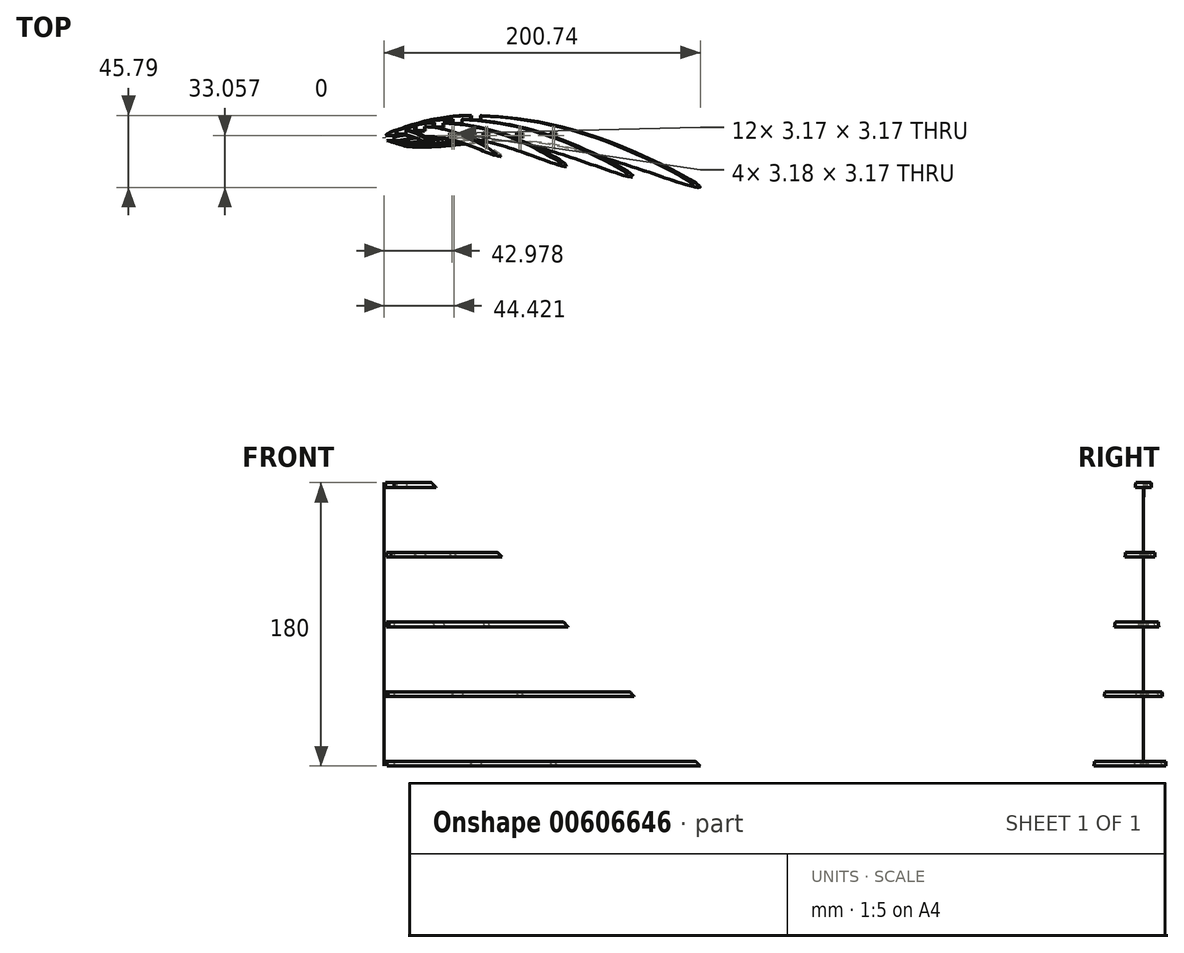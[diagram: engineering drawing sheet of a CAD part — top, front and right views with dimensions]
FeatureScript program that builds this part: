
annotation { "Feature Type Name" : "Feature", "Feature Type Description" : "" }
export const myFeature = defineFeature(function(context is Context, id is Id, definition is map)
    precondition{}
    {
        {
            var Q0;
            Q0=qCreatedBy(makeId("Top.planeOp"),FACE);
            var sketch = newSketch(context, id + "F0", { "sketchPlane" : qUnion([Q0])});
            skFitSpline(sketch, "E0", {"points": [v(6.7, -3.08) * mm, v(0, 0) * mm, v(27, 10.93) * mm, v(65.88, 14) * mm, v(142.55, -2.18) * mm, v(200.64, -31.37) * mm, v(115.71, -5.76) * mm, v(49.67, -4.11) * mm, v(16, -5.56) * mm, v(6.7, -3.08) * mm]});
            skLineSegment(sketch, "E1", {"start": v(52.43, 14.3) * mm, "end": v(52.43, 14.3) * mm});
            skSolve(sketch);
        }
        {
            var Q0;
            Q0=qCreatedBy(makeId("Top.planeOp"),FACE);
            cPlane(context, id + "F1", {"entities" : qUnion([Q0]), "cplaneType" : CPlaneType.OFFSET, "offset" : 180 * mm, "width" : 150 * mm, "height" : 150 * mm});
        }
        {
            var Q0;
            Q0=qCreatedBy(id+"F1.planeOp",FACE);
            var sketch = newSketch(context, id + "F2", { "sketchPlane" : qUnion([Q0])});
            skFitSpline(sketch, "E2", {"points": [v(0, 0) * mm, v(2.44, 2.88) * mm, v(10.73, 5.12) * mm, v(24.6, 0.41) * mm, v(30.02, -4.78) * mm, v(15.98, 1.36) * mm, v(4, -0.03) * mm, v(2.4, -0.47) * mm, v(0.9, -0.46) * mm, v(0, 0) * mm]});
            skSolve(sketch);
        }
        {
            var Q0;
            Q0=qCreatedBy(makeId("Right.planeOp"),FACE);
            var sketch = newSketch(context, id + "F3", { "sketchPlane" : qUnion([Q0])});
            skPoint(sketch, "E3.0", {"position": v(0, 180) * mm});
            skLineSegment(sketch, "E4", {"start": v(0, 180) * mm, "end": v(0, 0) * mm});
            skSolve(sketch);
        }
        {
            var Q0;
            Q0 = qSketchRegion(id + "F0", true);
            var Q1;
            Q1 = qSketchRegion(id + "F2", true);
            var Q2;
            Q2=sQuery(id+"F3.wireOp",EDGE,"E4");
            loft(context, id + "F4", {"addGuides" : true, "sheetProfilesArray" : [{ "sheetProfileEntities" : qUnion([Q0]) }, { "sheetProfileEntities" : qUnion([Q1]) }], "guidesArray" : [{ "guideEntities" : qUnion([Q2]), "guideDerivativeType" : LoftGuideDerivativeType.DEFAULT, "guideDerivativeMagnitude" : 1 }]});
        }
        {
            var Q0;
            Q0=makeQuery(id+"F2.imprint","IMPRINT",FACE,{"disambiguationData":[TD([[makeQuery(id+"F2.imprint","IMPRINT",EDGE,{"derivedFrom":sQuery(id+"F2.wireOp",EDGE,"E2")}),-1.0]])]});
            var sketch = newSketch(context, id + "F5", { "sketchPlane" : qUnion([Q0])});
            skLineSegment(sketch, "E5", {"start": v(10.64, 5.35) * mm, "end": v(13.82, 5.35) * mm});
            skLineSegment(sketch, "E6", {"start": v(13.82, 5.35) * mm, "end": v(13.82, 2.18) * mm});
            skLineSegment(sketch, "E7", {"start": v(13.82, 2.18) * mm, "end": v(7.47, 2.18) * mm});
            skLineSegment(sketch, "E8", {"start": v(7.47, 2.18) * mm, "end": v(7.47, 5.35) * mm});
            skLineSegment(sketch, "E9", {"start": v(7.47, 5.35) * mm, "end": v(10.64, 5.35) * mm});
            skSolve(sketch);
        }
        {
            var Q0;
            Q0=makeQuery(id+"F0.imprint","IMPRINT",FACE,{"disambiguationData":[TD([[makeQuery(id+"F0.imprint","IMPRINT",EDGE,{"derivedFrom":sQuery(id+"F0.wireOp",EDGE,"E0")}),-1.0]])]});
            var sketch = newSketch(context, id + "F6", { "sketchPlane" : qUnion([Q0])});
            skLineSegment(sketch, "E10", {"start": v(58.72, 14.54) * mm, "end": v(55.54, 14.54) * mm});
            skLineSegment(sketch, "E11", {"start": v(55.54, 14.54) * mm, "end": v(55.54, 11.36) * mm});
            skLineSegment(sketch, "E12", {"start": v(55.54, 11.36) * mm, "end": v(61.9, 11.36) * mm});
            skLineSegment(sketch, "E13", {"start": v(61.9, 11.36) * mm, "end": v(61.9, 14.54) * mm});
            skLineSegment(sketch, "E14", {"start": v(61.9, 14.54) * mm, "end": v(58.72, 14.54) * mm});
            skSolve(sketch);
        }
        {
            var Q0;
            Q0=sQuery(id+"F6.wireOp",VERTEX,"E11.start");
            var Q1;
            Q1=sQuery(id+"F6.wireOp",VERTEX,"E12.start");
            var Q2;
            Q2=sQuery(id+"F5.wireOp",VERTEX,"E8.start");
            cPlane(context, id + "F7", {"entities" : qUnion([Q0, Q1, Q2]), "cplaneType" : CPlaneType.THREE_POINT, "offset" : 25 * mm, "width" : 150 * mm, "height" : 150 * mm});
        }
        {
            var Q0;
            Q0=qCreatedBy(id+"F7.planeOp",FACE);
            var sketch = newSketch(context, id + "F8", { "sketchPlane" : qUnion([Q0])});
            skPoint(sketch, "E15.0", {"position": v(2.18, 171.98) * mm});
            skPoint(sketch, "E16.0", {"position": v(11.36, -14.33) * mm});
            skLineSegment(sketch, "E17", {"start": v(2.18, 171.98) * mm, "end": v(11.36, -14.33) * mm});
            skSolve(sketch);
        }
        {
            var Q0;
            Q0 = qSketchRegion(id + "F5", true);
            var Q1;
            Q1 = qSketchRegion(id + "F6", true);
            var Q2;
            Q2=sQuery(id+"F8.wireOp",EDGE,"E17");
            sweep(context, id + "F9", {"operationType" : NewBodyOperationType.REMOVE, "profiles" : qUnion([Q0, Q1]), "path" : qUnion([Q2])});
        }
        {
            var Q0;
            Q0=makeQuery(id+"F2.imprint","IMPRINT",FACE,{"disambiguationData":[TD([[makeQuery(id+"F2.imprint","IMPRINT",EDGE,{"derivedFrom":sQuery(id+"F2.wireOp",EDGE,"E2")}),-1.0]])]});
            var sketch = newSketch(context, id + "F10", { "sketchPlane" : qUnion([Q0])});
            skLineSegment(sketch, "E18", {"start": v(0, 0) * mm, "end": v(0, 1.59) * mm});
            skLineSegment(sketch, "E19", {"start": v(0, 1.59) * mm, "end": v(6.35, 1.59) * mm});
            skLineSegment(sketch, "E20", {"start": v(6.35, 1.59) * mm, "end": v(6.35, -1.59) * mm});
            skLineSegment(sketch, "E21", {"start": v(6.35, -1.59) * mm, "end": v(0, -1.59) * mm});
            skLineSegment(sketch, "E22", {"start": v(0, -1.59) * mm, "end": v(0, 0) * mm});
            skSolve(sketch);
        }
        {
            var Q0;
            Q0=makeQuery(id+"F0.imprint","IMPRINT",FACE,{"disambiguationData":[TD([[makeQuery(id+"F0.imprint","IMPRINT",EDGE,{"derivedFrom":sQuery(id+"F0.wireOp",EDGE,"E0")}),-1.0]])]});
            var sketch = newSketch(context, id + "F11", { "sketchPlane" : qUnion([Q0])});
            skLineSegment(sketch, "E23", {"start": v(0, 0) * mm, "end": v(0, 1.59) * mm});
            skLineSegment(sketch, "E24", {"start": v(0, 1.59) * mm, "end": v(3.18, 1.59) * mm});
            skLineSegment(sketch, "E25", {"start": v(3.18, 1.59) * mm, "end": v(3.18, -1.59) * mm});
            skLineSegment(sketch, "E26", {"start": v(3.18, -1.59) * mm, "end": v(0, -1.59) * mm});
            skLineSegment(sketch, "E27", {"start": v(0, -1.59) * mm, "end": v(0, 0) * mm});
            skSolve(sketch);
        }
        {
            var Q0;
            Q0=sQuery(id+"F11.wireOp",VERTEX,"E27.start");
            var Q1;
            Q1=sQuery(id+"F11.wireOp",VERTEX,"E24.start");
            var Q2;
            Q2=sQuery(id+"F10.wireOp",VERTEX,"E19.start");
            cPlane(context, id + "F12", {"entities" : qUnion([Q0, Q1, Q2]), "cplaneType" : CPlaneType.THREE_POINT, "offset" : 25 * mm, "width" : 150 * mm, "height" : 150 * mm});
        }
        {
            var Q0;
            Q0=qCreatedBy(id+"F12.planeOp",FACE);
            var sketch = newSketch(context, id + "F13", { "sketchPlane" : qUnion([Q0])});
            skPoint(sketch, "E28.0", {"position": v(-1.59, 180) * mm});
            skPoint(sketch, "E29.0", {"position": v(-1.59, 0) * mm});
            skLineSegment(sketch, "E30", {"start": v(-1.59, 0) * mm, "end": v(-1.59, 180) * mm});
            skSolve(sketch);
        }
        {
            var Q0;
            Q0 = qSketchRegion(id + "F11", true);
            var Q1;
            Q1 = qSketchRegion(id + "F10", true);
            var Q2;
            Q2=sQuery(id+"F13.wireOp",EDGE,"E30");
            sweep(context, id + "F14", {"operationType" : NewBodyOperationType.REMOVE, "profiles" : qUnion([Q0, Q1]), "path" : qUnion([Q2])});
        }
        {
            var Q0;
            Q0=qCreatedBy(makeId("Front.planeOp"),FACE);
            cPlane(context, id + "F15", {"entities" : qUnion([Q0]), "cplaneType" : CPlaneType.OFFSET, "offset" : 100 * mm, "width" : 150 * mm, "height" : 150 * mm});
        }
        {
            var Q0;
            Q0=qCreatedBy(id+"F15.planeOp",FACE);
            var sketch = newSketch(context, id + "F16", { "sketchPlane" : qUnion([Q0])});
            skLineSegment(sketch, "E31", {"start": v(0, 3) * mm, "end": v(0, 44.25) * mm});
            skLineSegment(sketch, "E32", {"start": v(0, 91.5) * mm, "end": v(0, 132.75) * mm});
            skLineSegment(sketch, "E33", {"start": v(0, 135.75) * mm, "end": v(0, 177) * mm});
            skLineSegment(sketch, "E34", {"start": v(0, 44.25) * mm, "end": v(212.22, 44.25) * mm});
            skLineSegment(sketch, "E35", {"start": v(0, 47.25) * mm, "end": v(188.49, 47.25) * mm});
            skLineSegment(sketch, "E36", {"start": v(0, 91.5) * mm, "end": v(130.22, 91.5) * mm});
            skLineSegment(sketch, "E37", {"start": v(0, 177) * mm, "end": v(111.2, 177) * mm});
            skLineSegment(sketch, "E38.bottom", {"start": v(111.2, 177) * mm, "end": v(0, 177) * mm});
            skLineSegment(sketch, "E38.top", {"start": v(111.2, 135.75) * mm, "end": v(0, 135.75) * mm});
            skLineSegment(sketch, "E38.left", {"start": v(111.2, 177) * mm, "end": v(111.2, 135.75) * mm});
            skLineSegment(sketch, "E39.bottom", {"start": v(130.22, 91.5) * mm, "end": v(0, 91.5) * mm});
            skLineSegment(sketch, "E39.top", {"start": v(130.22, 132.75) * mm, "end": v(0, 132.75) * mm});
            skLineSegment(sketch, "E39.left", {"start": v(130.22, 91.5) * mm, "end": v(130.22, 132.75) * mm});
            skLineSegment(sketch, "E40.bottom", {"start": v(188.49, 47.25) * mm, "end": v(0, 47.25) * mm});
            skLineSegment(sketch, "E40.top", {"start": v(188.49, 88.5) * mm, "end": v(0, 88.5) * mm});
            skLineSegment(sketch, "E40.left", {"start": v(188.49, 47.25) * mm, "end": v(188.49, 88.5) * mm});
            skLineSegment(sketch, "E40.right", {"start": v(0, 47.25) * mm, "end": v(0, 88.5) * mm});
            skLineSegment(sketch, "E41.bottom", {"start": v(0, 3) * mm, "end": v(212.22, 3) * mm});
            skLineSegment(sketch, "E41.right", {"start": v(212.22, 3) * mm, "end": v(212.22, 44.25) * mm});
            skSolve(sketch);
        }
        {
            var Q0;
            Q0 = qSketchRegion(id + "F16", true);
            extrude(context, id + "F17", {"entities" : qUnion([Q0]), "operationType" : NewBodyOperationType.REMOVE, "oppositeDirection" : true, "depth" : 200 * mm, "offsetDistance" : 25 * mm});
        }
        {
            var Q0;
            Q0=makeQuery(id+"F17.boolean.opBoolean","COPY",FACE,{"derivedFrom":makeQuery(id+"F17.opExtrude","SWEPT_FACE",FACE,{"disambiguationData":[OSD([sQuery(id+"F16.wireOp",EDGE,"E38.top")])]})});
            var sketch = newSketch(context, id + "F18", { "sketchPlane" : qUnion([Q0])});
            skLineSegment(sketch, "E42", {"start": v(41.38, 0) * mm, "end": v(41.38, 3.17) * mm});
            skLineSegment(sketch, "E43", {"start": v(41.38, 3.17) * mm, "end": v(44.56, 3.17) * mm});
            skLineSegment(sketch, "E44", {"start": v(44.56, 3.17) * mm, "end": v(44.56, 0) * mm});
            skLineSegment(sketch, "E45", {"start": v(44.56, 0) * mm, "end": v(41.38, 0) * mm});
            skSolve(sketch);
        }
        {
            var Q0;
            Q0=makeQuery(id+"F0.imprint","IMPRINT",FACE,{"disambiguationData":[TD([[makeQuery(id+"F0.imprint","IMPRINT",EDGE,{"derivedFrom":sQuery(id+"F0.wireOp",EDGE,"E0")}),-1.0]])]});
            var sketch = newSketch(context, id + "F19", { "sketchPlane" : qUnion([Q0])});
            skLineSegment(sketch, "E46", {"start": v(106.69, 0) * mm, "end": v(106.69, 3.18) * mm});
            skLineSegment(sketch, "E47", {"start": v(106.69, 3.18) * mm, "end": v(109.86, 3.18) * mm});
            skLineSegment(sketch, "E48", {"start": v(109.86, 3.17) * mm, "end": v(109.86, 0) * mm});
            skLineSegment(sketch, "E49", {"start": v(109.86, 0) * mm, "end": v(106.69, 0) * mm});
            skSolve(sketch);
        }
        {
            var Q0;
            Q0=sQuery(id+"F18.wireOp",VERTEX,"E44.start");
            var Q1;
            Q1=sQuery(id+"F18.wireOp",VERTEX,"E45.start");
            var Q2;
            Q2=sQuery(id+"F19.wireOp",VERTEX,"E49.start");
            cPlane(context, id + "F20", {"entities" : qUnion([Q0, Q1, Q2]), "cplaneType" : CPlaneType.THREE_POINT, "offset" : 25 * mm, "width" : 150 * mm, "height" : 150 * mm});
        }
        {
            var Q0;
            Q0=qCreatedBy(id+"F20.planeOp",FACE);
            var sketch = newSketch(context, id + "F21", { "sketchPlane" : qUnion([Q0])});
            skPoint(sketch, "E50.0", {"position": v(0, 103.01) * mm});
            skPoint(sketch, "E51.0", {"position": v(0, -47.63) * mm});
            skLineSegment(sketch, "E52", {"start": v(0, 103.01) * mm, "end": v(0, -47.63) * mm});
            skSolve(sketch);
        }
        {
            var Q0;
            Q0 = qSketchRegion(id + "F19", true);
            var Q1;
            Q1 = qSketchRegion(id + "F18", true);
            var Q2;
            Q2=sQuery(id+"F21.wireOp",EDGE,"E52");
            sweep(context, id + "F22", {"operationType" : NewBodyOperationType.REMOVE, "profiles" : qUnion([Q0, Q1]), "path" : qUnion([Q2])});
        }
    });
